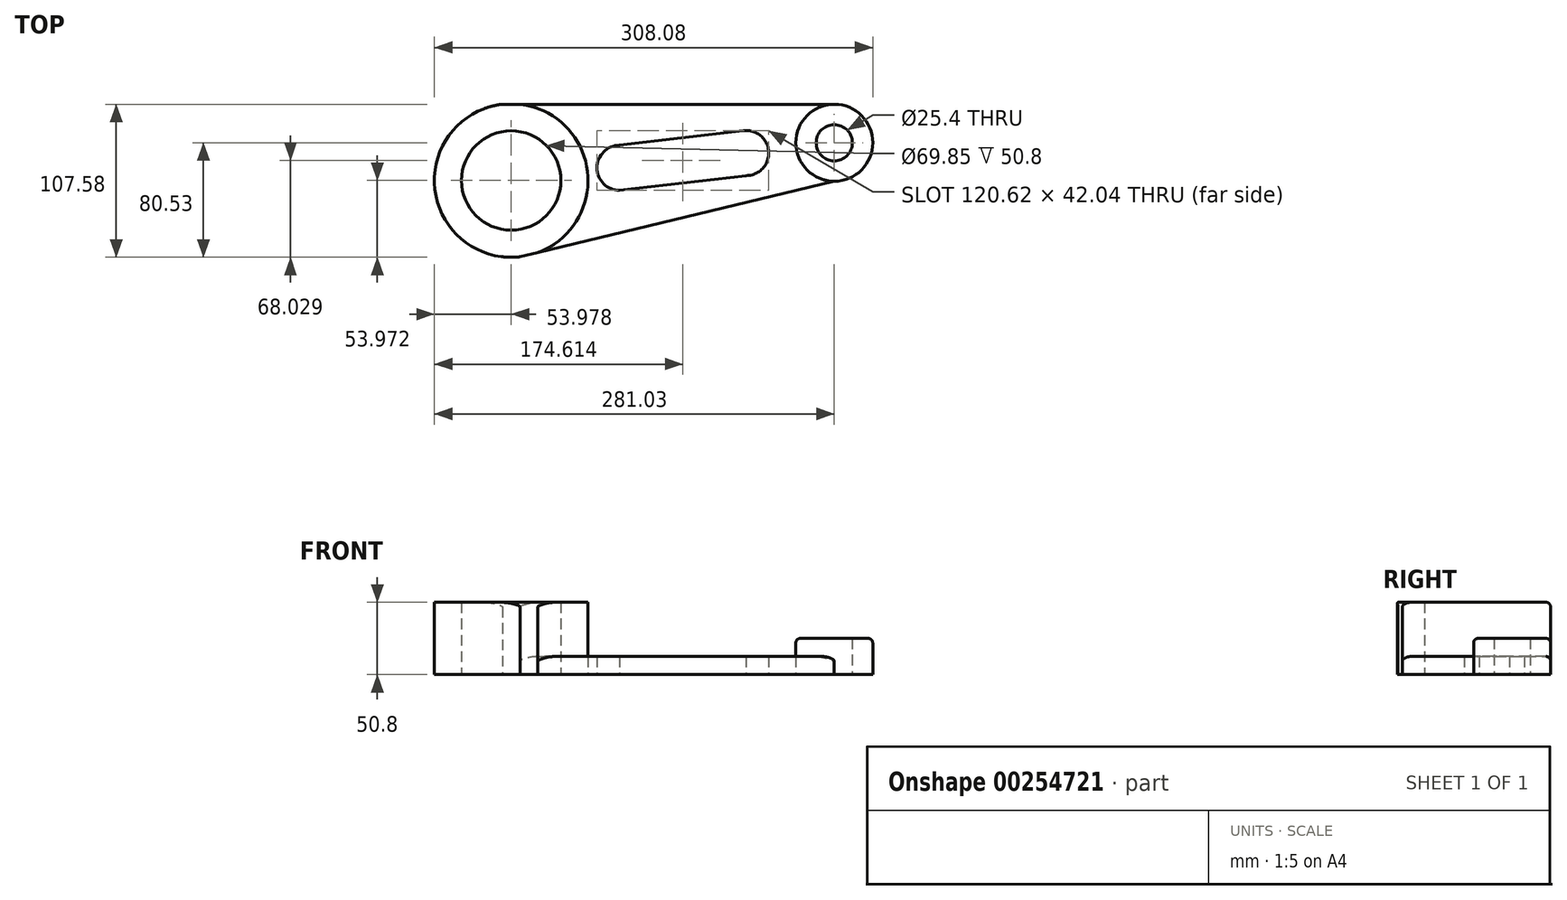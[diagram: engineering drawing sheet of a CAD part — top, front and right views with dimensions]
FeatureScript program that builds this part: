
annotation { "Feature Type Name" : "Feature", "Feature Type Description" : "" }
export const myFeature = defineFeature(function(context is Context, id is Id, definition is map)
    precondition{}
    {
        {
            var Q0;
            Q0=qCreatedBy(makeId("Top.planeOp"),FACE);
            var sketch = newSketch(context, id + "F0", { "sketchPlane" : qUnion([Q0])});
            skCircle(sketch, "E0", {"center": v(0, 0) * mm, "radius": 12.7 * mm});
            skCircle(sketch, "E1", {"center": v(0, 0) * mm, "radius": 27.05 * mm});
            skCircle(sketch, "E2", {"center": v(-227.05, -26.56) * mm, "radius": 34.93 * mm});
            skCircle(sketch, "E3", {"center": v(-227.05, -26.56) * mm, "radius": 53.98 * mm});
            skArc(sketch, "E4", {"start": v(-150.85, -1.77) * mm, "mid": v(-166.73, -17.65) * mm, "end": v(-150.85, -33.52) * mm});
            skArc(sketch, "E5", {"start": v(-61.95, -23.12) * mm, "mid": v(-46.1, -6.31) * mm, "end": v(-63.82, 8.52) * mm});
            skLineSegment(sketch, "E6", {"start": v(-150.85, -1.77) * mm, "end": v(-63.82, 8.52) * mm});
            skLineSegment(sketch, "E7.MirrorCS", {"start": v(-150.85, -33.52) * mm, "end": v(-61.95, -23.12) * mm});
            skLineSegment(sketch, "E8", {"start": v(-233.32, 27.05) * mm, "end": v(0, 27.05) * mm});
            skLineSegment(sketch, "E9.MirrorCS", {"start": v(-220.78, -80.17) * mm, "end": v(0, -27.05) * mm});
            skSolve(sketch);
        }
        {
            var Q0;
            Q0=makeQuery(id+"F0.imprint","IMPRINT",FACE,{"disambiguationData":[TD([[makeQuery(id+"F0.imprint","IMPRINT",EDGE,{"derivedFrom":sQuery(id+"F0.wireOp",EDGE,"E2")}),-1.0]])]});
            extrude(context, id + "F1", {"entities" : qUnion([Q0]), "depth" : 50.8 * mm});
        }
        {
            var Q0;
            Q0=makeQuery(id+"F0.imprint","IMPRINT",FACE,{"disambiguationData":[TD([[makeQuery(id+"F0.imprint","IMPRINT",EDGE,{"derivedFrom":sQuery(id+"F0.wireOp",EDGE,"E0")}),-1.0]])]});
            extrude(context, id + "F2", {"entities" : qUnion([Q0]), "depth" : 25.4 * mm});
        }
        {
            var Q0;
            Q0=makeQuery(id+"F0.imprint","IMPRINT",FACE,{"disambiguationData":[TD([[makeQuery(id+"F0.imprint","IMPRINT",EDGE,{"derivedFrom":sQuery(id+"F0.wireOp",EDGE,"E4")}),-1.0]])]});
            extrude(context, id + "F3", {"entities" : qUnion([Q0]), "depth" : 12.7 * mm});
        }
        {
            var Q0;
            {var subQ0=sQuery(id+"F0.wireOp",EDGE,"E3");Q0=makeQuery(id+"F1.opExtrude","CAP_EDGE",EDGE,{"disambiguationData":[OSD([subQ0]),TDD([makeQuery(id+"F0.imprint","IMPRINT",EDGE,{"disambiguationData":[TD([[makeQuery(id+"F0.imprint","INTERSECT",VERTEX,{"disambiguationData":[OD(1.0)],"derivedFrom":[subQ0,sQuery(id+"F0.wireOp",EDGE,"E8")]}),1.0]])],"derivedFrom":subQ0})])],"isStart":false});}
            var Q1;
            Q1=makeQuery(id+"F1.opExtrude","CAP_EDGE",EDGE,{"disambiguationData":[OSD([sQuery(id+"F0.wireOp",EDGE,"E9.MirrorCS")])],"isStart":false});
            var Q2;
            {var subQ0=sQuery(id+"F0.wireOp",EDGE,"E3");Q2=makeQuery(id+"F1.opExtrude","CAP_EDGE",EDGE,{"disambiguationData":[OSD([subQ0]),TDD([makeQuery(id+"F0.imprint","IMPRINT",EDGE,{"disambiguationData":[TD([[makeQuery(id+"F0.imprint","INTERSECT",VERTEX,{"disambiguationData":[OD(0.0)],"derivedFrom":[subQ0,sQuery(id+"F0.wireOp",EDGE,"E8")]}),-1.0]])],"derivedFrom":subQ0})])],"isStart":false});}
            var Q3;
            Q3=makeQuery(id+"F1.opExtrude","CAP_EDGE",EDGE,{"disambiguationData":[OSD([sQuery(id+"F0.wireOp",EDGE,"E8")])],"isStart":false});
            var Q4;
            Q4=makeQuery(id+"F3.opExtrude","CAP_EDGE",EDGE,{"disambiguationData":[OSD([sQuery(id+"F0.wireOp",EDGE,"E8")])],"isStart":false});
            var Q5;
            Q5=makeQuery(id+"F3.opExtrude","CAP_EDGE",EDGE,{"disambiguationData":[OSD([sQuery(id+"F0.wireOp",EDGE,"E9.MirrorCS")])],"isStart":false});
            var Q6;
            Q6=makeQuery(id+"F2.opExtrude","CAP_EDGE",EDGE,{"disambiguationData":[OSD([sQuery(id+"F0.wireOp",EDGE,"E1")])],"isStart":false});
            fillet(context, id + "F4", {"entities" : qUnion([Q0, Q1, Q2, Q3, Q4, Q5, Q6]), "radius" : 3.17 * mm, "tangentPropagation" : true, "allowEdgeOverflow" : false});
        }
    });
